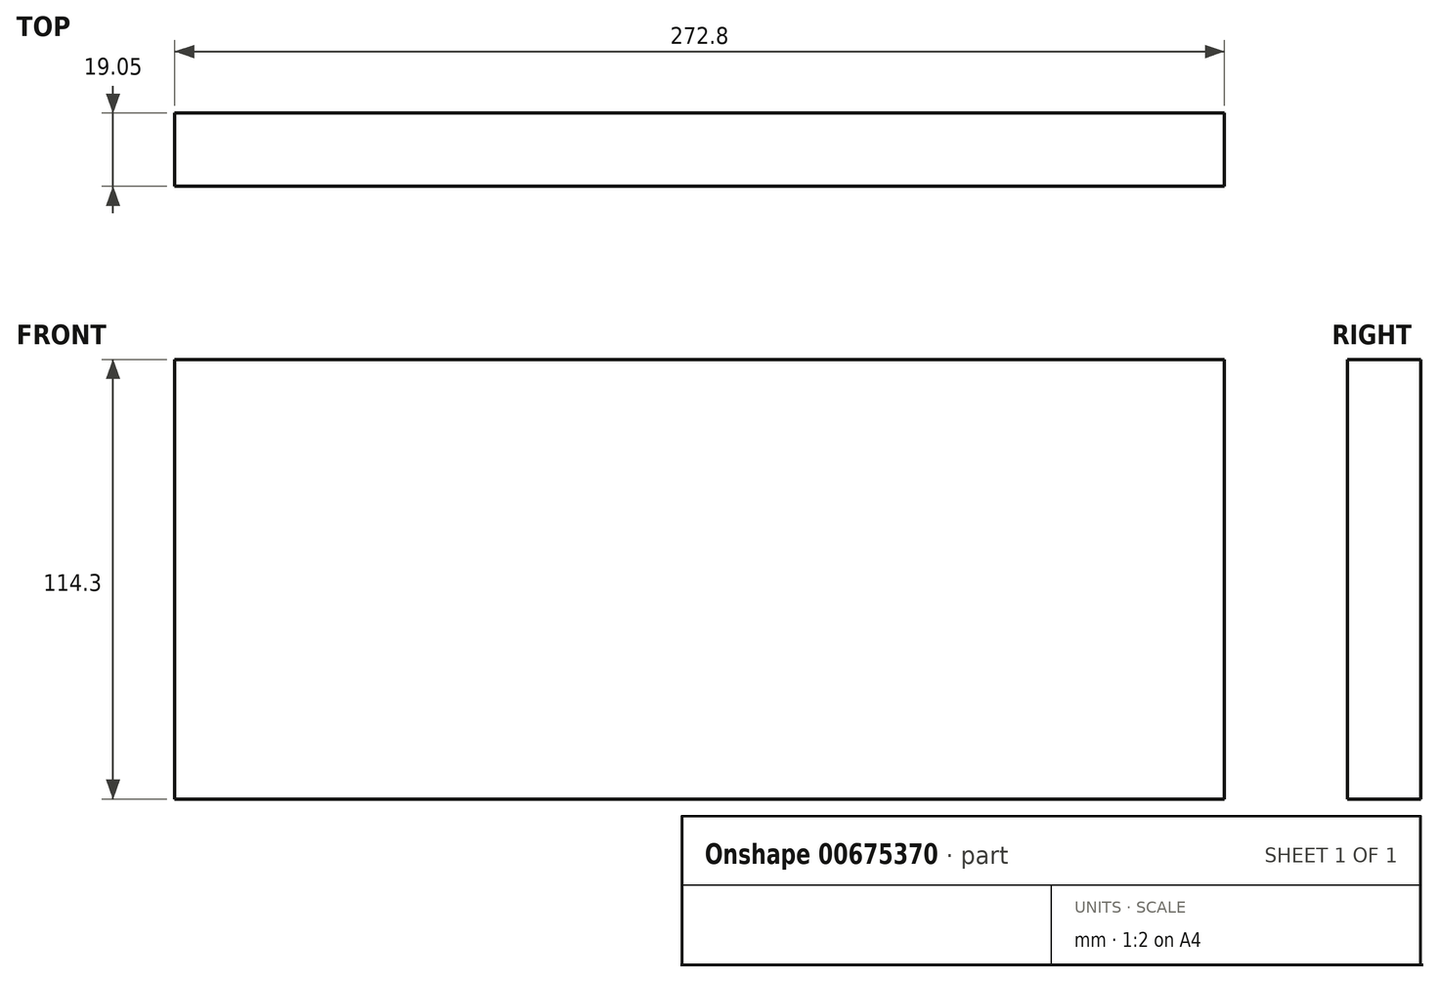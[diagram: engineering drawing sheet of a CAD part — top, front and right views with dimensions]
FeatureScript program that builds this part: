
annotation { "Feature Type Name" : "Feature", "Feature Type Description" : "" }
export const myFeature = defineFeature(function(context is Context, id is Id, definition is map)
    precondition{}
    {
        {
            var Q0;
            Q0=qCreatedBy(makeId("Front.planeOp"),FACE);
            var sketch = newSketch(context, id + "F0", { "sketchPlane" : qUnion([Q0])});
            skLineSegment(sketch, "E0.bottom", {"start": v(0, 0) * mm, "end": v(272.8, 0) * mm});
            skLineSegment(sketch, "E0.top", {"start": v(0, 114.3) * mm, "end": v(272.8, 114.3) * mm});
            skLineSegment(sketch, "E0.left", {"start": v(0, 0) * mm, "end": v(0, 114.3) * mm});
            skLineSegment(sketch, "E0.right", {"start": v(272.8, 0) * mm, "end": v(272.8, 114.3) * mm});
            skSolve(sketch);
        }
        {
            var Q0;
            Q0=makeQuery(id+"F0.imprint","IMPRINT",FACE,{"disambiguationData":[TD([[makeQuery(id+"F0.imprint","IMPRINT",EDGE,{"derivedFrom":sQuery(id+"F0.wireOp",EDGE,"E0.bottom")}),1.0]])]});
            extrude(context, id + "F1", {"entities" : qUnion([Q0]), "depth" : 19.05 * mm, "offsetDistance" : 25.4 * mm});
        }
    });
